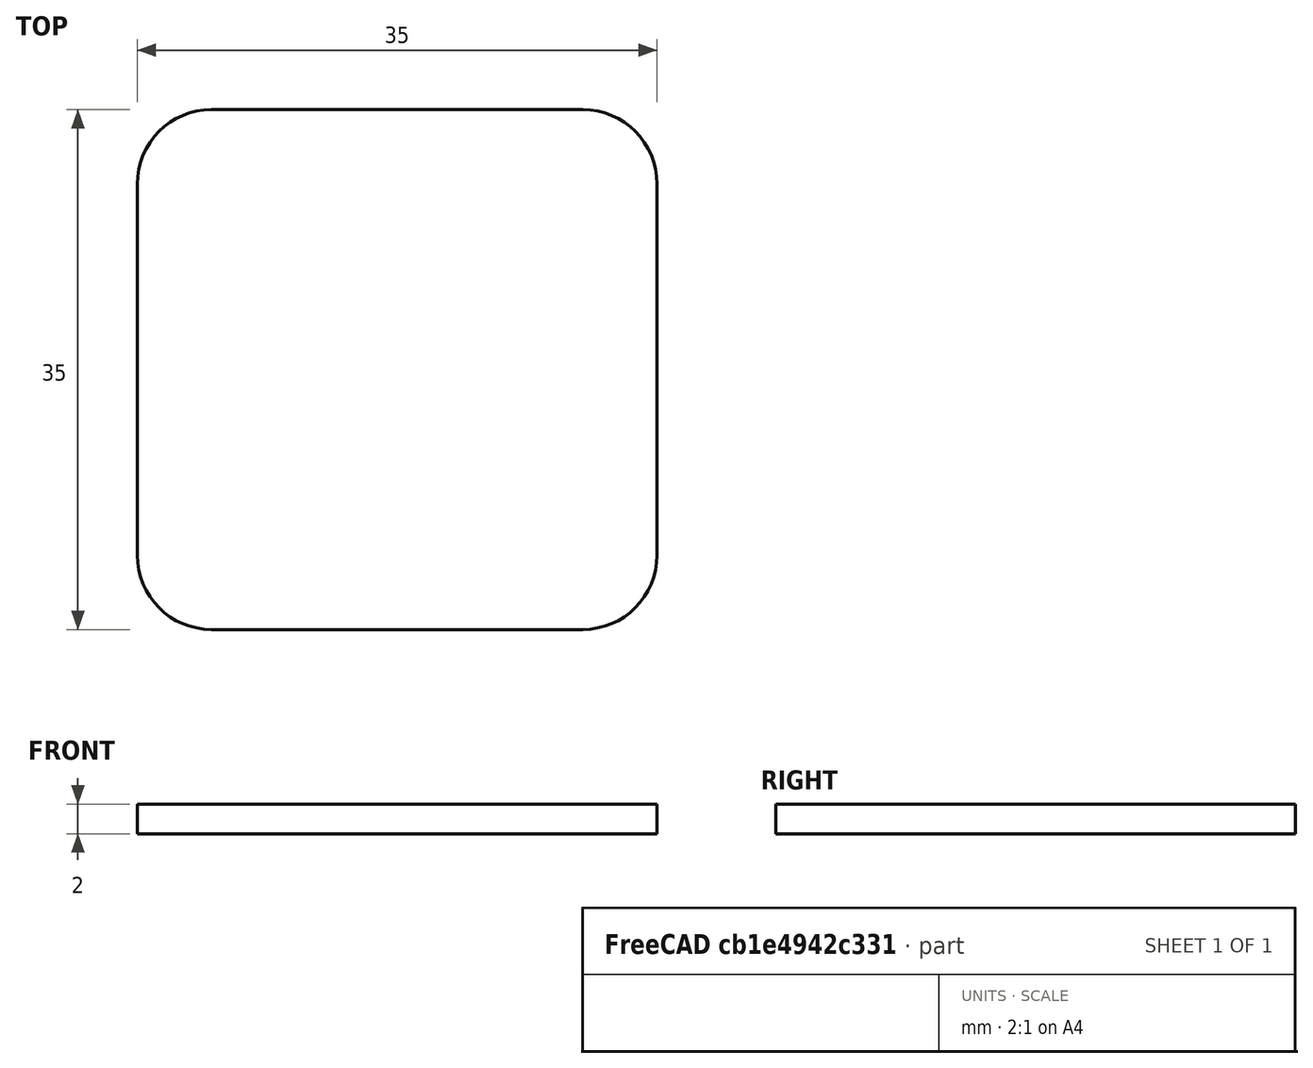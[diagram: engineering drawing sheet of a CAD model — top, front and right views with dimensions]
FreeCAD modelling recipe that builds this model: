
FCSTD DOCUMENT  (FreeCAD 1.0R39285 (Git))
Label: AqaraTH
License: All rights reserved
LicenseURL: https://en.wikipedia.org/wiki/All_rights_reserved
objects: Sketcher::SketchObject×1, PartDesign::Pad×1, PartDesign::Body×1
note: 6 computed .brp shape members not serialized (recipe doc carries the construction recipe); baked Part::Feature solids carry a one-line shape summary decoded from their .brp

FEATURE [Sketcher::SketchObject] Sketch
  ArcFitTolerance = 1e-06
  AttachmentSupport = -> [XY_Plane]
  FullyConstrained = true
  MakeInternals = false
  MapMode = 5
  sketch-geometry (13):
    g0: LineSegment StartX=-17.5 StartY=12.5 StartZ=0 EndX=-17.5 EndY=-12.5 EndZ=0
    g1: LineSegment StartX=-12.5 StartY=-17.5 StartZ=0 EndX=12.5 EndY=-17.5 EndZ=0
    g2: LineSegment StartX=17.5 StartY=-12.5 StartZ=0 EndX=17.5 EndY=12.5 EndZ=0
    g3: LineSegment StartX=12.5 StartY=17.5 StartZ=0 EndX=-12.5 EndY=17.5 EndZ=0
    g4: GeomPoint [constr] X=0 Y=0 Z=0
    g5: ArcOfCircle CenterX=-12.5 CenterY=12.5 CenterZ=0 NormalX=0 NormalY=0 NormalZ=1 AngleXU=0 Radius=5 StartAngle=1.5708 EndAngle=3.14159
    g6: GeomPoint [constr] X=-17.5 Y=17.5 Z=0
    g7: ArcOfCircle CenterX=12.5 CenterY=12.5 CenterZ=0 NormalX=0 NormalY=0 NormalZ=1 AngleXU=0 Radius=5 StartAngle=1e-16 EndAngle=1.5708
    g8: GeomPoint [constr] X=17.5 Y=17.5 Z=0
    g9: ArcOfCircle CenterX=12.5 CenterY=-12.5 CenterZ=0 NormalX=0 NormalY=0 NormalZ=1 AngleXU=0 Radius=5 StartAngle=4.71239 EndAngle=6.28319
    g10: GeomPoint [constr] X=17.5 Y=-17.5 Z=0
    g11: ArcOfCircle CenterX=-12.5 CenterY=-12.5 CenterZ=0 NormalX=0 NormalY=0 NormalZ=1 AngleXU=0 Radius=5 StartAngle=3.14159 EndAngle=4.71239
    g12: GeomPoint [constr] X=-17.5 Y=-17.5 Z=0
  constraints (28):
    c: Vertical(g0)
    c: Vertical(g2)
    c: Horizontal(g1)
    c: Horizontal(g3)
    c: Symmetric(g10,g6,g4)
    c: Coincident(g4,g-1)
    c: DistanceX(g6,g8) = 35
    c: DistanceY(g10,g8) = 35
    c: PointOnObject(g6,g0)
    c: PointOnObject(g6,g3)
    c: Tangent(g0,g5) = -1.5708
    c: Tangent(g3,g5) = -1.5708
    c: PointOnObject(g8,g3)
    c: PointOnObject(g8,g2)
    c: Tangent(g3,g7) = -1.5708
    c: Tangent(g2,g7) = -1.5708
    c: PointOnObject(g10,g2)
    c: PointOnObject(g10,g1)
    c: Tangent(g2,g9) = -1.5708
    c: Tangent(g1,g9) = -1.5708
    c: PointOnObject(g12,g1)
    c: PointOnObject(g12,g0)
    c: Tangent(g1,g11) = -1.5708
    c: Tangent(g0,g11) = -1.5708
    c: Radius(g5) = 5
    c: Radius(g7) = 5
    c: Radius(g9) = 5
    c: Radius(g11) = 5
FEATURE [PartDesign::Pad] Pad
  Direction = (0,0,1)
  Length = 2
  Length2 = 10
  Profile = -> Sketch
  ReferenceAxis = -> Sketch [N_Axis]
  Refine = true
  Suppressed = false
  Type = 0
FEATURE [PartDesign::Body] Body
  AllowCompound = false
  Group = -> [Sketch,Pad]
  Origin = -> Origin
  Tip = -> Pad
